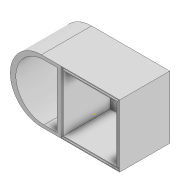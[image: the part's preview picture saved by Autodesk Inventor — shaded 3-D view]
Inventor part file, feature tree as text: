
AUTODESK INVENTOR PART (.ipt)
format: ipt  version: 2020 (Build 240168000, 168)  size: 187,904 bytes
history: native  units: mm
features: sketch x12, extrude x6
ambient origin geometry x8: Origin, YZ Plane, XZ Plane, XY Plane, X Axis, Y Axis, Z Axis, Center Point
bodies: Volumenkörper1 (feature_tree)
feature tree (18):
  extrude  "Extrusion1"  Depth=200.0mm
  sketch  "Skizze2"  dims[d2=10.0mm d3=10.0mm]
  sketch  "Skizze3"  dims[d4=10.0mm d5=10.0mm]
  sketch  "Skizze4"  dims[d6=150.0mm d7=0.0mm d9=10.0mm]
  sketch  "Skizze5"  dims[d10=10.0mm d11=150.0mm d12=0.0mm]
  sketch  "Skizze6"  dims[d13=10.0mm d14=0.0mm d15=10.0mm d16=0.0mm]
  extrude  "Extrusion2"  Depth=10.0mm
  extrude  "Extrusion3"  Depth=10.0mm
  extrude  "Extrusion4"  Depth=10.0mm
  sketch  "Skizze10"  dims[d20=2.5mm]
  extrude  "Extrusion5"  Depth=150.0mm TaperAngle=0.0deg
  extrude  "Extrusion6"  Depth=10.0mm TaperAngle=0.0deg
  sketch  "Skizze1"  dims[d0=200.0mm d1=200.0mm]
  sketch  "Skizze7"  dims[d17=2.5mm]
  sketch  "Skizze8"  dims[d18=2.5mm]
  sketch  "Skizze9"  dims[d19=2.5mm]
  sketch  "Skizze11"  dims[d21=2.5mm]
  sketch  "Skizze12"  dims[d22=2.5mm d23=2.5mm d24=2.5mm d25=5.0mm d26=5.0mm d27=5.0mm d28=0.0mm d29=90.0mm d30=85.0mm d31=5.0mm d32=5.0mm d33=5.0mm d34=5.0mm d35=5.0mm d36=0.0mm]
